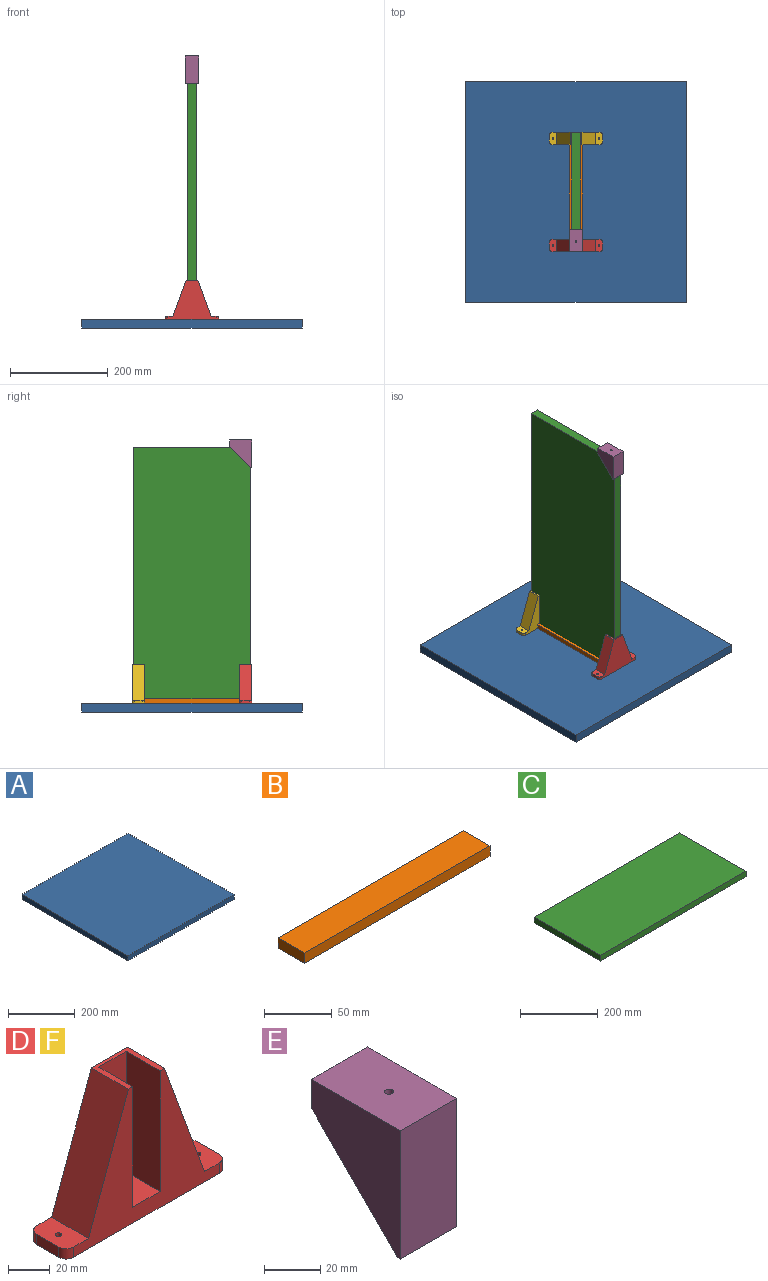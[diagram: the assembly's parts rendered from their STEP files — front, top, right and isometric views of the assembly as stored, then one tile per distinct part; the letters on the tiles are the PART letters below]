
ASSEMBLY  parts=6 mates=5
PART A: 6 faces, bbox 450x450x18 mm
  f0: plane 450x18mm, normal (0,1,0), area 8100mm2, adj f1,f3,f4,f5
  f1: plane 450x18mm, normal (-1,0,0), area 8100mm2, adj f0,f2,f4,f5
  f2: plane 450x18mm, normal (0,-1,0), area 8100mm2, adj f1,f3,f4,f5
  f3: plane 450x18mm, normal (1,0,0), area 8100mm2, adj f0,f2,f4,f5
  f4: plane 450x450mm, normal (0,0,1), area 202500mm2, adj f0,f1,f2,f3
  f5: plane 450x450mm, normal (0,0,-1), area 202500mm2, adj f0,f1,f2,f3
PART B: 6 faces, bbox 194x27.5x9.4 mm
  f0: plane 194x9.35mm, normal (0,1,0), area 1813.9mm2, adj f1,f3,f4,f5
  f1: plane 27.5x9.35mm, normal (-1,0,0), area 257.1mm2, adj f0,f2,f4,f5
  f2: plane 194x9.35mm, normal (0,-1,0), area 1813.9mm2, adj f1,f3,f4,f5
  f3: plane 27.5x9.35mm, normal (1,0,0), area 257.1mm2, adj f0,f2,f4,f5
  f4: plane 194x27.5mm, normal (0,0,1), area 5335mm2, adj f0,f1,f2,f3
  f5: plane 194x27.5mm, normal (0,0,-1), area 5335mm2, adj f0,f1,f2,f3
PART C: 6 faces, bbox 529x240x18 mm
  f0: plane 529x18mm, normal (0,1,0), area 9522mm2, adj f1,f3,f4,f5
  f1: plane 240x18mm, normal (-1,0,0), area 4320mm2, adj f0,f2,f4,f5
  f2: plane 529x18mm, normal (0,-1,0), area 9522mm2, adj f1,f3,f4,f5
  f3: plane 240x18mm, normal (1,0,0), area 4320mm2, adj f0,f2,f4,f5
  f4: plane 529x240mm, normal (0,0,1), area 126960mm2, adj f0,f1,f2,f3
  f5: plane 529x240mm, normal (0,0,-1), area 126960mm2, adj f0,f1,f2,f3
PART D: 20 faces, bbox 108.5x25x80 mm
  f0: plane 23x18.5mm, normal (0,0,1), area 425.5mm2, adj f1,f10,f11,f13
  f1: plane 70.65x23mm, normal (1,0,0), area 1625mm2, adj f0,f9,f11,f13
  f2: plane 74x27mm, normal (-0.94,0,0.34), area 1969.3mm2, adj f3,f9,f11,f12
  f3: plane 25x15mm, normal (0,0,1), area 357.2mm2, adj f2,f4,f11,f12,f15,f16,f19
  f4: plane 15x6mm, normal (-1,0,0), area 90mm2, adj f3,f5,f15,f16
  f5: plane 108.5x25mm, normal (0,0,-1), area 2676.9mm2, adj f4,f6,f11,f12,f14,f15,f16,f17
  f6: plane 15x6mm, normal (1,0,0), area 90mm2, adj f5,f7,f14,f17
  f7: plane 25x15mm, normal (0,0,1), area 357.2mm2, adj f6,f8,f11,f12,f14,f17,f18
  f8: plane 74x27mm, normal (0.94,0,0.34), area 1969.3mm2, adj f7,f9,f11,f12
  f9: plane 25x24.5mm, normal (0,0,1), area 187mm2, adj f1,f2,f8,f10,f11,f12,f13
  f10: plane 70.65x23mm, normal (-1,0,0), area 1625mm2, adj f0,f9,f11,f13
  f11: plane 98.5x80mm, normal (0,-1,0), area 3095mm2, adj f0,f1,f2,f3,f5,f7,f8,f9
  f12: plane 98.5x80mm, normal (0,1,0), area 4402mm2, adj f2,f3,f5,f7,f8,f9,f14,f15
  f13: plane 70.65x18.5mm, normal (0,-1,0), area 1307mm2, adj f0,f1,f9,f10
  f14: cylinder r=5mm len=6mm, axis (0,0,1), area 47.1mm2, adj f5,f6,f7,f12
  f15: cylinder r=5mm len=6mm, axis (0,0,-1), area 47.1mm2, adj f3,f4,f5,f12
  f16: cylinder r=5mm len=6mm, axis (0,0,1), area 47.1mm2, adj f3,f4,f5,f11
  f17: cylinder r=5mm len=6mm, axis (0,0,-1), area 47.1mm2, adj f5,f6,f7,f11
  f18: cylinder r=1.5mm len=6mm, axis (0,0,1), area 56.5mm2, adj f5,f7
  f19: cylinder r=1.5mm len=6mm, axis (0,0,1), area 56.5mm2, adj f3,f5
PART E: 12 faces, bbox 28.3x45x56 mm
  f0: plane 56x28.3mm, normal (0,-1,0), area 1584.8mm2, adj f1,f2,f9,f11
  f1: plane 56x45mm, normal (1,0,0), area 1573.9mm2, adj f0,f3,f8,f9,f11
  f2: plane 56x45mm, normal (-1,0,0), area 1573.9mm2, adj f0,f3,f8,f9,f11
  f3: plane 43.5x43.5mm, normal (0,0.71,-0.71), area 332mm2, adj f1,f2,f4,f5,f6,f7,f8,f11
  f4: plane 41x24.3mm, normal (0,1,0), area 996.3mm2, adj f3,f5,f6,f7
  f5: plane 41x24.3mm, normal (0,0,-1), area 988.3mm2, adj f3,f4,f6,f7,f10
  f6: plane 41x41mm, normal (-1,0,0), area 840.5mm2, adj f3,f4,f5
  f7: plane 41x41mm, normal (1,0,0), area 840.5mm2, adj f3,f4,f5
  f8: plane 28.3x12.5mm, normal (0,1,0), area 353.8mm2, adj f1,f2,f3,f9
  f9: plane 45x28.3mm, normal (0,0,1), area 1265.5mm2, adj f0,f1,f2,f8,f10
  f10: cylinder r=1.6mm len=14.5mm, axis (0,0,1), area 145.8mm2, adj f5,f9
  f11: plane 28.3x1.5mm, normal (0,0,-1), area 42.4mm2, adj f0,f1,f2,f3
PART F: same geometry as D
PLACE A t=(4.51,-92.09,-35.79)mm
PLACE B rot(axis=(0,0,-1),90deg) t=(4.51,-92.09,-17.79)mm
PLACE C rot(axis=(0,1,0),90deg) t=(-4.49,-81.15,238.64)mm
PLACE D rot(axis=(0,0,1),180deg) t=(4.51,-214.09,22.21)mm
PLACE E t=(-9.64,-214.09,462.57)mm
PLACE F t=(4.51,29.91,22.21)mm fixed
MATE fastened D.f11 <-> B.f3  axis (0,1,0) through (4.51,-189.09,-17.79)mm
MATE fastened E.f4 <-> C.f2  axis (0,1,0) through (4.51,-212.09,505.57)mm
MATE slider C.f3 <-> B.f4  axis (0,0,-1) through (4.51,-92.09,-23.43)mm
MATE fastened B.f5 <-> A.f4  axis (0,0,-1) through (4.51,-92.09,-17.79)mm
MATE fastened B.f1 <-> F.f11  axis (0,1,0) through (4.51,4.91,-17.79)mm
